# Revit family: Building-IEC309Connections-GEWISS-67IB-INTERLOCKED-SOCKET-OUTLETS_IP67_WITHOUT_BOTTOM_63A
name_source: partatom
category: Apparecchi elettrici
revit_build: Autodesk Revit 2016 (Build: 20161004_0715(x64)
units: mm (PartAtom-declared; Revit-internal decimal feet)

## family parameters
Condiviso = No
Host = Muro
Mantenere orientamento annotazione = Sì
Numero OmniClass = 23.80.50.14
Punto di calcolo locali = No
Quota connettore circolare = Usa diametro
Sempre verticale = Sì
Taglio con vuoti quando caricato = No
Tipo di parte = Normale
Titolo OmniClass = Plug Connectors

## types (11) — shared parameters
Altezza da terra = 1112 mm
Carico apparente = 0 VA
Catalogue = BUILDING
Catalogue Range = 67 IB
Classificazione carico = Altro
Electrocod = 2222
Frequency = 50/60 Hz
Glow Wire Test = 850 °C
Glow wire test: = 850 °C
IDF = 122861de-0204-44ac-8832-c9cd502636ad
IDT = 3210f2e1-5490-4980-ba84-a365430e0752
IP degree = IP67
Immagine tipo = GW67365N.jpg
Numero poli = 3
Operating temperature: = -25 +40 °C
Potenza = 500 V
Presa = GEWISS - NERO
Produttore = GEWISS S.p.A.
Protection = NO (SBF)
Rated current (A) = 63
Rated current (In) = 63
Rated frequency (Hz) = 50/60 Hz
SEO = Socket outlet
Shock resistance = IK08
Struttura = GEWISS - Grigio RAL - 7035
Struttura frontale = GEWISS -BLU
Technical sheet = https://www.gewiss.com
Thermo-pressure with ball = 125
Tipo Simbolo = PRESAINDSTAGNA : 3P
Typology = Vertical
URL = https://www.gewiss.com
Version file RFA = 18.0
Vetro = GEWISS - vetro
With back-mounting box = No
Working temperature = -25 ÷ +40 °C

## per-type parameters (varying)
| type | Colour | Colour: | Descrizione | EAN code | Modello | No. of poles | Number of poles | Rated voltage | Rated voltage: | Reference h |
| GW67356N - 63A 2P+E 110V V.INT.SOCK.O.N.B.4H SBF | Yellow | Yellow | 63A 2P+E 110V V.INT.SOCK.O.N.B.4H SBF | 8011564742376 | GW67356N | 2P+E | 2P+E | 100 - 130 V | 100 - 130 V | 4 |
| GW67357N - 63A 3P+E 110V V.INT.SOCK.O.N.B.4H SBF | Yellow | Yellow | 63A 3P+E 110V V.INT.SOCK.O.N.B.4H SBF | 8011564742383 | GW67357N | 3P+E | 3P+E | 100 - 130 V | 100 - 130 V | 4 |
| GW67361N - 63A 3P+N+E 220V V.INT.SOCK.O.N.B.9H SBF | Blue | Blue | 63A 3P+N+E 220V V.INT.SOCK.O.N.B.9H SBF | 8011564742420 | GW67361N | 3P+N+E | 3P+N+E | 200 - 250 V | 200 - 250 V | 9 |
| GW67358N - 63A 3P+N+E 110V V.INT.SOCK.O.N.B.4H SBF | Yellow | Yellow | 63A 3P+N+E 110V V.INT.SOCK.O.N.B.4H SBF | 8011564742390 | GW67358N | 3P+N+E | 3P+N+E | 100 - 130 V | 100 - 130 V | 4 |
| GW67360N - 63A 3P+E 220V V.INT.SOCK.O.N.B.9H SBF | Blue | Blue | 63A 3P+E 220V V.INT.SOCK.O.N.B.9H SBF | 8011564742413 | GW67360N | 3P+E | 3P+E | 200 - 250 V | 200 - 250 V | 9 |
| GW67363N - 63A 3P+E 380V V.INT.SOCK.O.N.B.6H SBF | Red | Red | 63A 3P+E 380V V.INT.SOCK.O.N.B.6H SBF | 8011564742444 | GW67363N | 3P+E | 3P+E | 380 - 415 V | 380 - 415 V | 6 |
| GW67366N - 63A 3P+N+E 500V V.INT.SOCK.O.N.B.7H SBF | Black | Black | 63A 3P+N+E 500V V.INT.SOCK.O.N.B.7H SBF | 8011564742475 | GW67366N | 3P+N+E | 3P+N+E | 480 - 500 V | 480 - 500 V | 7 |
| GW67364N - 63A 3P+N+E 380V V.INT.SOCK.O.N.B.6H SBF | Red | Red | 63A 3P+N+E 380V V.INT.SOCK.O.N.B.6H SBF | 8011564742451 | GW67364N | 3P+N+E | 3P+N+E | 380 - 415 V | 380 - 415 V | 6 |
| GW67359N - 63A 2P+E 220V V.INT.SOCK.O.N.B.6H SBF | Blue | Blue | 63A 2P+E 220V V.INT.SOCK.O.N.B.6H SBF | 8011564742406 | GW67359N | 2P+E | 2P+E | 200 - 250 V | 200 - 250 V | 6 |
| GW67365N - 63A 3P+E 500V V.INT.SOCK.O.N.B.7H SBF | Black | Black | 63A 3P+E 500V V.INT.SOCK.O.N.B.7H SBF | 8011564742468 | GW67365N | 3P+E | 3P+E | 480 - 500 V | 480 - 500 V | 7 |
| GW67362N - 63A 2P+E 380V V.INT.SOCK.O.N.B.9H SBF | Red | Red | 63A 2P+E 380V V.INT.SOCK.O.N.B.9H SBF | 8011564742437 | GW67362N | 2P+E | 2P+E | 380 - 415 V | 380 - 415 V | 9 |

note: source unit labels omitted for Thermo-pressure with ball — the stored unit's dimension contradicts the parameter name (converter mislabeling)

## geometry (parser evidence)
native form markers: Sweep x2
no freeform markers — native parametric forms only
